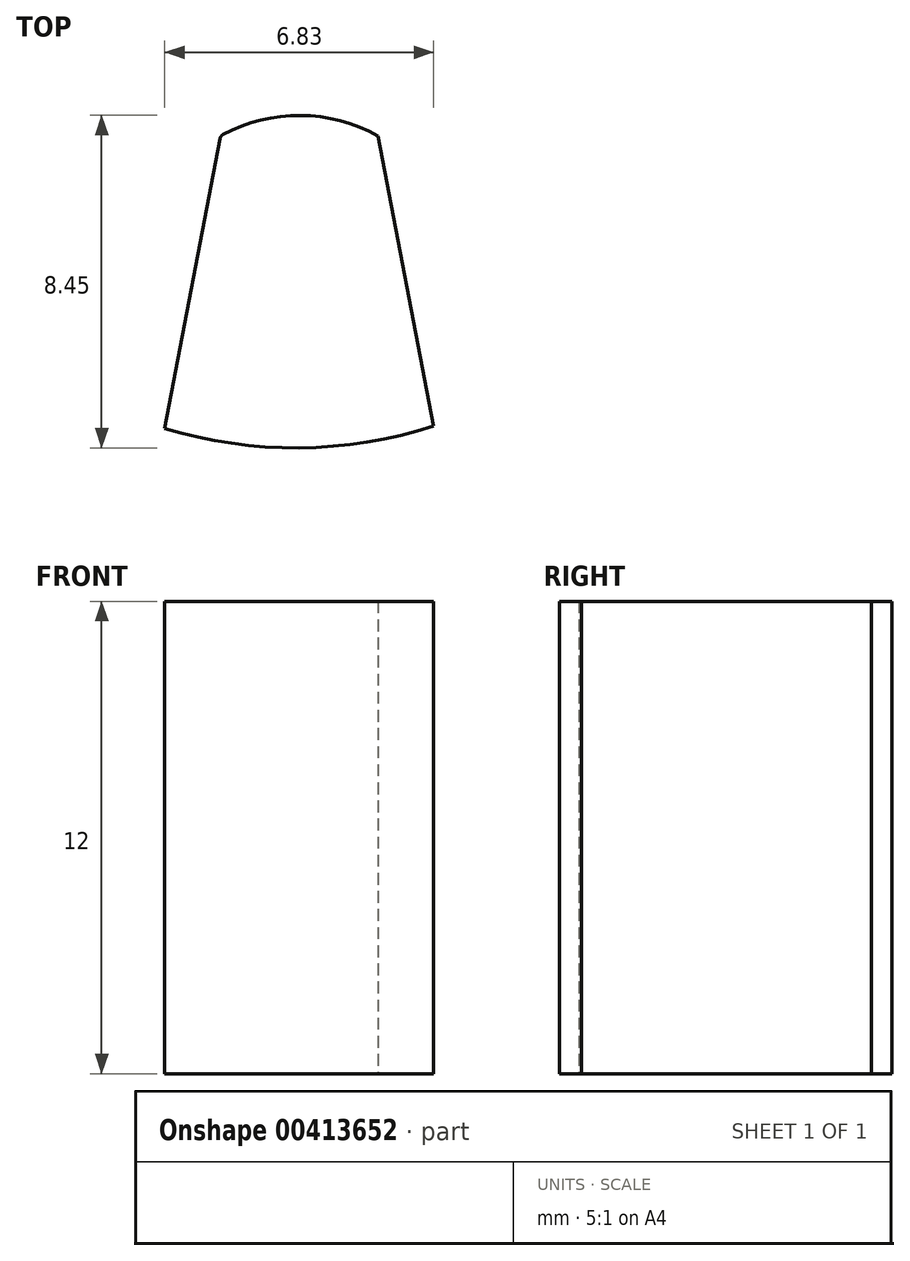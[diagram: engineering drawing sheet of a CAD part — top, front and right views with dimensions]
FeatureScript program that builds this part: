
annotation { "Feature Type Name" : "Feature", "Feature Type Description" : "" }
export const myFeature = defineFeature(function(context is Context, id is Id, definition is map)
    precondition{}
    {
        {
            var Q0;
            Q0=qCreatedBy(makeId("Top.planeOp"),FACE);
            var sketch = newSketch(context, id + "F0", { "sketchPlane" : qUnion([Q0])});
            skPoint(sketch, "E0.end.orphan", {"position": v(0.4, -1.28) * mm});
            skArc(sketch, "E1", {"start": v(2.4, 2.6) * mm, "mid": v(0.43, 3.12) * mm, "end": v(-1.55, 2.62) * mm});
            skPoint(sketch, "E2.start.orphan", {"position": v(0.4, 2.69) * mm});
            skArc(sketch, "E3", {"start": v(-3.02, -4.83) * mm, "mid": v(0.4, -5.33) * mm, "end": v(3.8, -4.77) * mm});
            skPoint(sketch, "E4.trimOffspring.start.orphan", {"position": v(0.4, -5.25) * mm});
            skLineSegment(sketch, "E5", {"start": v(-1.61, 2.53) * mm, "end": v(-3.02, -4.83) * mm});
            skLineSegment(sketch, "E6", {"start": v(2.4, 2.6) * mm, "end": v(3.8, -4.77) * mm});
            skPoint(sketch, "E7.start.orphan", {"position": v(0.4, 3.12) * mm});
            skPoint(sketch, "E8.visualSharp", {"position": v(-1.6, 2.6) * mm});
            skArc(sketch, "E8.filletArc", {"start": v(-1.55, 2.62) * mm, "mid": v(-1.6, 2.59) * mm, "end": v(-1.61, 2.53) * mm});
            skSolve(sketch);
        }
        {
            var Q0;
            Q0=makeQuery(id+"F0.imprint","IMPRINT",FACE,{"disambiguationData":[TD([[makeQuery(id+"F0.imprint","IMPRINT",EDGE,{"derivedFrom":sQuery(id+"F0.wireOp",EDGE,"E1")}),1.0]])]});
            extrude(context, id + "F1", {"entities" : qUnion([Q0]), "depth" : 12 * mm});
        }
    });
